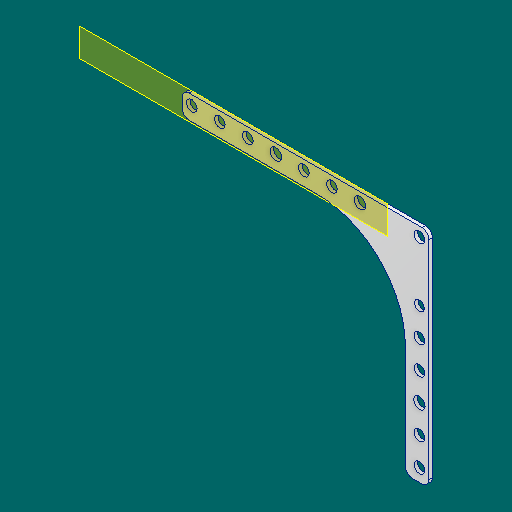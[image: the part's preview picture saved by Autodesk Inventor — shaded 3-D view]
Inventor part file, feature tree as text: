
AUTODESK INVENTOR PART (.ipt)
format: ipt  version: 2023.1 (Build 271208000, 208)  size: 145,920 bytes
history: native  units: in
note: dims shown in document units (in); Inventor stores cm internally (conversion verified against a paired STEP export)
features: other x3, sketch x1, plane x1
ambient origin geometry x8: Origin, YZ Plane, XZ Plane, XY Plane, X Axis, Y Axis, Z Axis, Center Point
bodies: Solid1 (feature_tree)
feature tree (5):
  other  "UnderGusset.ipt"
  other  "Solid1::UnderGusset.ipt"
  other  "TaggingFeature1"
  sketch  "Sketch1"  dims[d0=0.3937in]
  plane  "Work Plane1"
